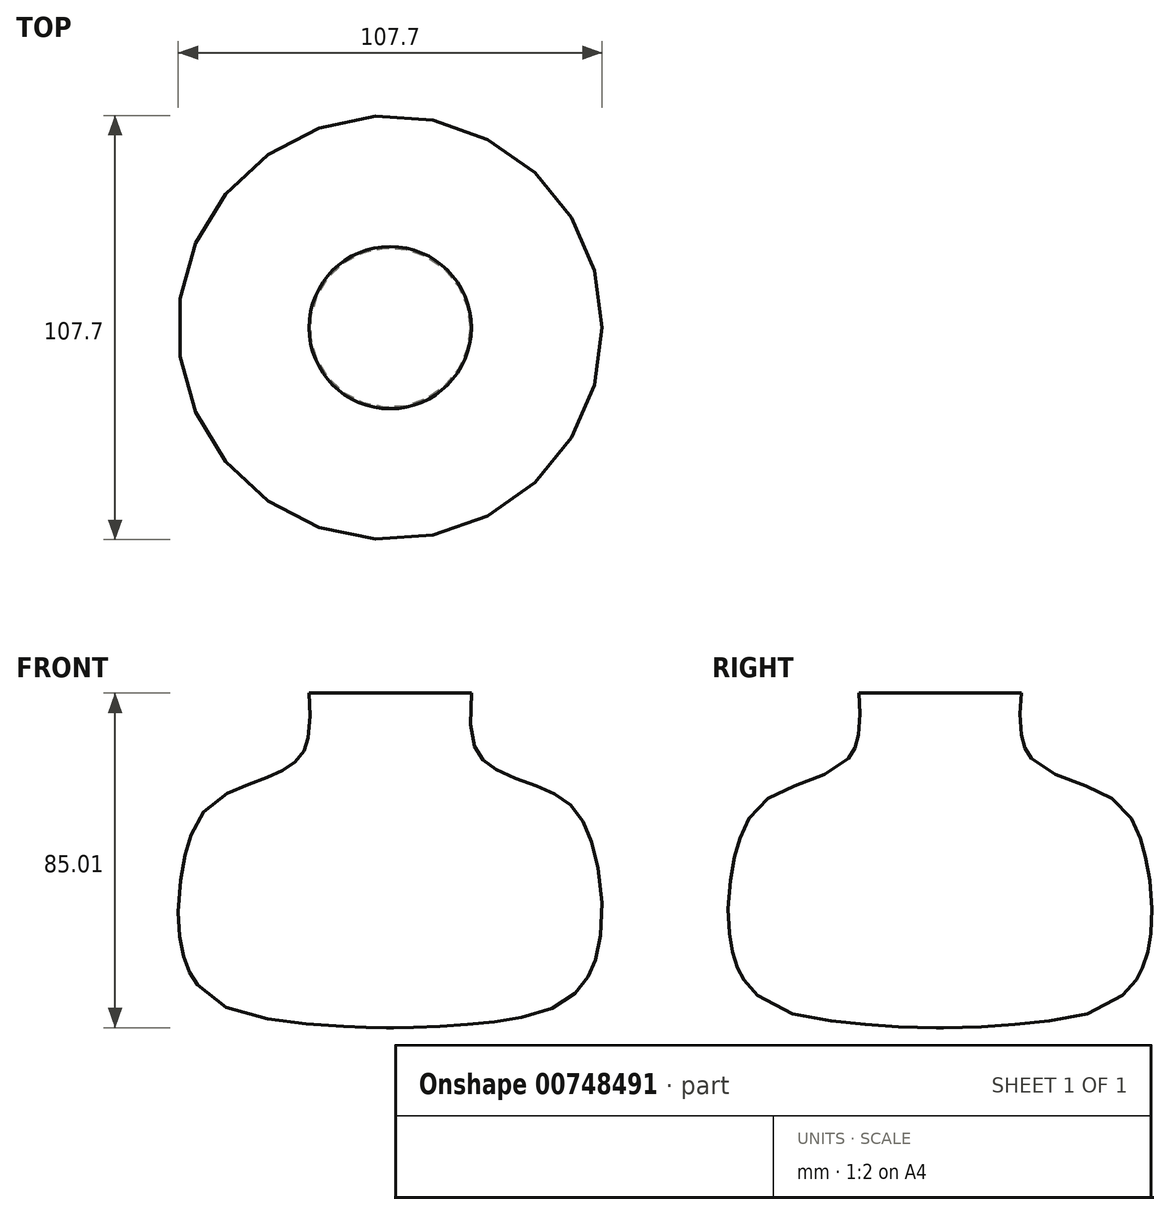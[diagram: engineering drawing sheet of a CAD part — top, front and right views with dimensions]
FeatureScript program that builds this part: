
annotation { "Feature Type Name" : "Feature", "Feature Type Description" : "" }
export const myFeature = defineFeature(function(context is Context, id is Id, definition is map)
    precondition{}
    {
        {
            var Q0;
            Q0=qCreatedBy(makeId("Front.planeOp"),FACE);
            var sketch = newSketch(context, id + "F0", { "sketchPlane" : qUnion([Q0])});
            skFitSpline(sketch, "E0", {"points": [v(18.05, 43.1) * mm, v(20.78, 20.05) * mm, v(39.65, 10.43) * mm, v(48.18, 0) * mm, v(48.18, -31.3) * mm, v(23.86, -42.37) * mm, v(-5.72, -43.1) * mm, v(-5.53, -42.73) * mm], "startDerivative": vector(-15.85, -165.33) * mm, "endDerivative": vector(18.58, 17.87) * mm});
            skFitSpline(sketch, "E1.0", {"points": [v(21.04, 42.8) * mm, v(20.88, 41.09) * mm, v(20.55, 37.68) * mm, v(20.3, 32.87) * mm, v(20.46, 29.27) * mm, v(20.88, 26.74) * mm, v(21.35, 25.05) * mm, v(21.98, 23.57) * mm, v(22.64, 22.5) * mm, v(23.26, 21.74) * mm, v(23.8, 21.19) * mm, v(24.41, 20.65) * mm, v(25.32, 19.95) * mm, v(26.63, 19.12) * mm, v(28.42, 18.19) * mm, v(30.37, 17.32) * mm, v(32.42, 16.5) * mm, v(34.53, 15.72) * mm, v(36.65, 14.94) * mm, v(38.72, 14.14) * mm, v(40.38, 13.42) * mm, v(41.64, 12.8) * mm, v(42.86, 12.13) * mm, v(44.27, 11.2) * mm, v(45.82, 9.94) * mm, v(47.2, 8.5) * mm, v(48.39, 6.86) * mm, v(49.4, 5.06) * mm, v(50.29, 3.1) * mm, v(51.05, 0.93) * mm, v(51.74, -1.45) * mm, v(52.55, -4.9) * mm, v(53.35, -9.63) * mm, v(53.83, -15.67) * mm, v(53.73, -20.74) * mm, v(53.28, -24.67) * mm, v(52.73, -27.52) * mm, v(52.07, -29.78) * mm, v(51.4, -31.51) * mm, v(50.82, -32.76) * mm, v(50.16, -33.95) * mm, v(49.19, -35.44) * mm, v(47.79, -37.13) * mm, v(45.86, -38.87) * mm, v(43, -40.82) * mm, v(38.98, -42.62) * mm, v(34.45, -43.82) * mm, v(30.53, -44.54) * mm, v(27.45, -44.98) * mm, v(24.22, -45.36) * mm, v(20.85, -45.68) * mm, v(17.4, -45.96) * mm, v(13.92, -46.2) * mm, v(10.5, -46.38) * mm, v(7.2, -46.51) * mm, v(4.63, -46.59) * mm, v(2.7, -46.62) * mm, v(1.34, -46.63) * mm, v(0.05, -46.63) * mm, v(-1.14, -46.61) * mm, v(-2.24, -46.58) * mm, v(-3.24, -46.54) * mm, v(-3.98, -46.49) * mm, v(-4.53, -46.44) * mm, v(-4.92, -46.4) * mm, v(-5.29, -46.34) * mm, v(-5.65, -46.28) * mm, v(-6.01, -46.2) * mm, v(-6.34, -46.11) * mm, v(-6.65, -46) * mm, v(-6.91, -45.88) * mm, v(-7.23, -45.71) * mm, v(-7.55, -45.5) * mm, v(-7.84, -45.23) * mm, v(-8.07, -44.97) * mm, v(-8.3, -44.64) * mm, v(-8.56, -44.14) * mm, v(-8.76, -43.4) * mm, v(-8.74, -42.55) * mm, v(-8.56, -41.91) * mm, v(-8.34, -41.47) * mm, v(-8.14, -41.16) * mm, v(-7.92, -40.88) * mm, v(-7.72, -40.67) * mm, v(-7.64, -40.6) * mm, v(-7.61, -40.57) * mm]});
            skLineSegment(sketch, "E2", {"start": v(-5.72, 38.38) * mm, "end": v(26.76, 38.38) * mm});
            skLineSegment(sketch, "E3", {"start": v(0, 40.37) * mm, "end": v(0, -51.08) * mm});
            skSolve(sketch);
        }
        {
            var Q0;
            {var subQ0=sQuery(id+"F0.wireOp",EDGE,"E2");var subQ1=sQuery(id+"F0.wireOp",EDGE,"E0");var subQ2=makeQuery(id+"F0.imprint","INTERSECT",VERTEX,{"derivedFrom":[subQ1,subQ0]});Q0=makeQuery(id+"F0.imprint","IMPRINT",FACE,{"disambiguationData":[TD([[makeQuery(id+"F0.imprint","IMPRINT",EDGE,{"disambiguationData":[TD([[subQ2,-1.0]])],"derivedFrom":subQ1}),-1.0]])]});}
            var Q1;
            {var subQ0=sQuery(id+"F0.wireOp",EDGE,"E2");var subQ1=sQuery(id+"F0.wireOp",EDGE,"E0");var subQ2=makeQuery(id+"F0.imprint","INTERSECT",VERTEX,{"derivedFrom":[subQ1,subQ0]});Q1=makeQuery(id+"F0.imprint","IMPRINT",FACE,{"disambiguationData":[TD([[makeQuery(id+"F0.imprint","IMPRINT",EDGE,{"disambiguationData":[TD([[subQ2,-1.0]])],"derivedFrom":subQ1}),1.0]])]});}
            var Q2;
            Q2=sQuery(id+"F0.wireOp",EDGE,"E3");
            revolve(context, id + "F1", {"surfaceOperationType" : NewSurfaceOperationType.NEW, "entities" : qUnion([Q0, Q1]), "axis" : qUnion([Q2]), "revolveType" : RevolveType.FULL});
        }
    });
